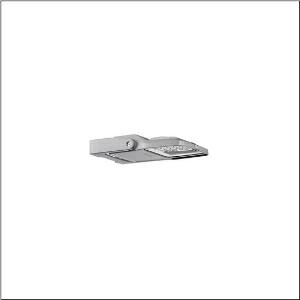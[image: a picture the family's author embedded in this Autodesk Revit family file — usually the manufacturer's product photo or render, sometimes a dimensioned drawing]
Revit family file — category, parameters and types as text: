
# Revit family: floodlight_fl_21_iq_micro___pl52_5xa7761a2d2a_1372
name_source: partatom
category: Lighting Fixtures
units: mm (PartAtom-declared; Revit-internal decimal feet)

## family parameters
Cut with Voids When Loaded = No
Host = Face
Light Source = No
Part Type = Normal
Room Calculation Point = No
Round Connector Dimension = Use Diameter
Shared = No

## types (1)
- --- (1 x LED, 2890 lm, 23.1 W, 3000K)
    Apparent Load = 23 VA
    CIE Flux Codes = 26 60 98 100 100
    Color Rendering = 70
    Color Temperature = 3000K
    Default Elevation = 1800 mm
    Description = Floodlight FL 21 iQ micro, floodlight, primary light control with lens, of PMMA, primary optical cover: protective disc, of toughened safety glass, transparent, light distribution: PL52, light emission: direct distribution, installation type: surface-mounted, LED, High Power LED, rated luminous flux: 2.890lm, luminous efficacy: 125lm/W, light colour: 730, colour temperature: 3000K, control: optimised constant luminous flux control (CLO 2.0), Desk-Remote (wireless, voltage-free reading and setting of iQ features in the workshop via application-optimized NFC function/RFID function), Light-Fading, Smart-Wire, Night-Set, Lumen-Switch, Temp-Guard, Auto-Match, with terminal, 6-pole, mains connection: 220..240V, AC, 50/60Hz, start of lifetime: 23W, end of service life: 24W, reduction: 11W, luminaire housing, of diecast aluminium, powder-coated, Siteco® metallic grey (DB 702S), corrosivity category C5 mid according to DIN EN ISO 12944, sealing non-destructively replaceable, design bracket, of diecast aluminium, powder-coated, Siteco® metallic grey (DB 702S), protection rating (complete): IP66, insulation class (complete): insulation class II (safety insulation), certification: CE, ENEC, VDE, protection symbol: D, impact resistance: IK07, permissible operating ambient temperature: -40..+40°C, permissible operating ambient temperature for outdoor applications: -40..+50°C, standard: DIN EN 12944, LABS conformity tested according to VDMA 24364:2018-05, packaging unit: 1 piece

Light Distribution: PL52
    Height = 65 mm
    Lamp = 1 x LED
    Lamp Light Flux = 2890 lm
    Lamp Power = 23.1 W
    Lamp count = 1
    Length = 312 mm
    Luminous efficacy = 125 lm/W
    Manufacturer = Siteco
    ModVariant = No
    Model = 5XA7761A2D2A
    Mounting Place = Wall
    Mounting Type = Surface mounted
    Number of Poles = 1
    OnlyDefault = Yes
    Power Factor = 1
    Product Name = Floodlight FL 21 iQ micro | PL52
    Product group = floodlight | wall mounted
    ProductGroupID = 2001
    Protection Class = Protection class II
    Protection Degree = IP 66
    RLX_Detail_Level = 1
    RLX_Emergency_Light_Flux = 0 lm
    RLX_Emergency_Type = 0
    RLX_Emergency_Type_DB = No
    RlxData = <blob elided: 97509 chars, md5=d63f2a08>
    Socket = socket
    Standby Power = 0 W
    System Light Flux = 2890 lm
    System Power = 23 W
    Type Comments = factory setting: luminous flux: 100 % | dim-lin: 254 | 455 mA
    Type Image = l_1006878.jpg
    URL = http://relux.com
    VarID = @adj_110921
    Voltage = 0 V
    Weight = 0.00 kg
    Width = 230 mm

## geometry (parser evidence)
native form markers: Blend x4, Sweep x13
no freeform markers — native parametric forms only
